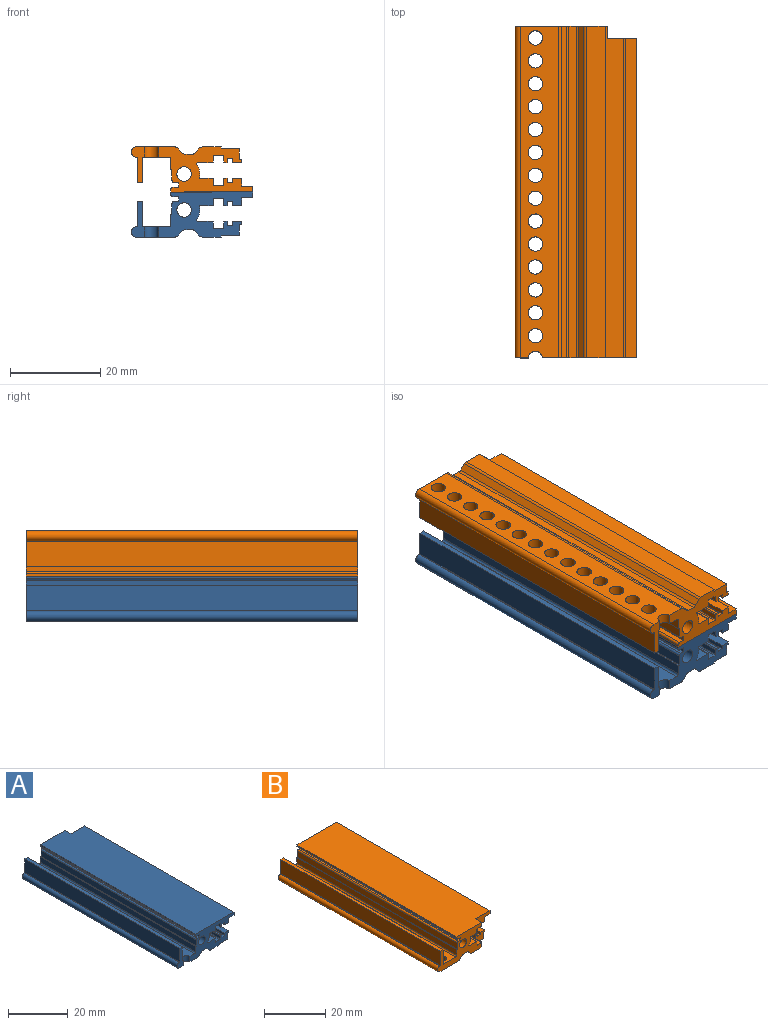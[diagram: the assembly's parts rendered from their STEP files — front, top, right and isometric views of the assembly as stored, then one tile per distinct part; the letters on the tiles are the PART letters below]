
ASSEMBLY  parts=2 mates=1
PART A: 86 faces, bbox 27x73.6x10 mm
  f0: plane 73.6x18.25mm, normal (0,0,1), area 1325mm2, adj f36,f57,f58,f59,f60,f62
  f1: cylinder r=1.6mm len=73.6mm, axis (0,1,0), area 739.9mm2, adj f36,f58
  f2: plane 73.6x1.13mm, normal (0.71,0,-0.71), area 117.8mm2, adj f3,f35,f36,f58
  f3: cylinder r=0.8mm len=73.6mm, axis (0,-1,0), area 46.2mm2, adj f2,f4,f36,f58
  f4: plane 73.6x1.64mm, normal (0,0,-1), area 120.5mm2, adj f3,f5,f36,f58
  f5: cylinder r=0.8mm len=73.6mm, axis (0,-1,0), area 46.2mm2, adj f4,f6,f36,f58
  f6: plane 73.6x1.13mm, normal (-0.71,0,-0.71), area 117.8mm2, adj f5,f36,f37,f58
  f7: cylinder r=1.6mm len=3.18mm, axis (0,0,-1), area 10.6mm2, adj f9,f38,f58,f85
  f8: plane 73.6x0.23mm, normal (0,0,1), area 16.6mm2, adj f10,f36,f55,f85
  f9: plane 73.6x5.7mm, normal (0,0,1), area 303.4mm2, adj f7,f11,f12,f36,f40,f41,f42,f43
  f10: plane 73.6x5.65mm, normal (-1,0,0), area 415.8mm2, adj f8,f36,f54,f85
  f11: plane 73.6x5.65mm, normal (1,0,0), area 415.8mm2, adj f9,f36,f54,f85
  f12: cylinder r=0.5mm len=73.6mm, axis (0,-1,0), area 57.8mm2, adj f9,f13,f36,f58
  f13: plane 73.6x2.25mm, normal (-1,0,0), area 165.6mm2, adj f12,f14,f36,f58
  f14: plane 73.6x0.3mm, normal (0,0,1), area 22.1mm2, adj f13,f15,f36,f58
  f15: plane 73.6x2.4mm, normal (-1,0,0), area 176.6mm2, adj f14,f16,f36,f58
  f16: cylinder r=0.5mm len=73.6mm, axis (0,-1,0), area 57.8mm2, adj f15,f17,f36,f58
  f17: plane 73.6x1mm, normal (0,0,1), area 73.6mm2, adj f16,f18,f36,f58
  f18: plane 73.6x1.1mm, normal (-1,0,0), area 81mm2, adj f17,f19,f36,f58
  f19: plane 73.6x1.3mm, normal (0,0,-1), area 95.7mm2, adj f18,f36,f56,f58
  f20: cylinder r=0.2mm len=73.6mm, axis (0,1,0), area 23.1mm2, adj f34,f36,f58,f62,f64
  f21: plane 73.6x4mm, normal (0,0,-1), area 284.6mm2, adj f22,f36,f58,f61,f63,f80
  f22: plane 73.6x0.4mm, normal (1,0,0), area 29.4mm2, adj f21,f36,f39,f58
  f23: cylinder r=0.2mm len=73.6mm, axis (0,1,0), area 23.1mm2, adj f24,f36,f58,f63,f82
  f24: plane 73.6x1.9mm, normal (0,0,1), area 139.8mm2, adj f23,f25,f36,f58
  f25: cylinder r=0.2mm len=73.6mm, axis (0,1,0), area 23.1mm2, adj f24,f26,f36,f58
  f26: plane 73.6x1.2mm, normal (1,0,0), area 88.3mm2, adj f25,f36,f58,f83
  f27: plane 73.6x3.31mm, normal (0,0,1), area 243.8mm2, adj f28,f36,f58,f83
  f28: cylinder r=0.2mm len=73.6mm, axis (0,1,0), area 32.7mm2, adj f27,f29,f36,f58
  f29: cylinder r=3.5mm len=73.6mm, axis (0,1,0), area 221mm2, adj f28,f30,f36,f58
  f30: cylinder r=0.2mm len=73.6mm, axis (0,1,0), area 26.1mm2, adj f29,f31,f36,f58
  f31: plane 73.6x2.63mm, normal (0,0,-1), area 193.3mm2, adj f30,f36,f58,f84
  f32: plane 73.6x1.2mm, normal (1,0,0), area 88.3mm2, adj f33,f36,f58,f84
  f33: cylinder r=0.2mm len=73.6mm, axis (0,1,0), area 23.1mm2, adj f32,f34,f36,f58
  f34: plane 73.6x1.9mm, normal (0,0,-1), area 139.8mm2, adj f20,f33,f36,f58
  f35: cylinder r=0.8mm len=73.6mm, axis (0,-1,0), area 46.2mm2, adj f2,f36,f38,f58
  f36: plane 20.5x10mm, normal (0,1,0), area 100.1mm2, adj f0,f1,f2,f3,f4,f5,f6,f8
  f37: cylinder r=0.8mm len=73.6mm, axis (0,1,0), area 46.2mm2, adj f6,f36,f39,f58
  f38: plane 73.6x8.54mm, normal (0,0,-1), area 512.7mm2, adj f7,f35,f36,f40,f41,f42,f43,f44
  f39: plane 73.6x4.17mm, normal (0,0,-1), area 306.8mm2, adj f22,f36,f37,f58
  f40: cylinder r=1.6mm len=3.2mm, axis (0,0,-1), area 22.6mm2, adj f9,f38
  f41: cylinder r=1.6mm len=3.2mm, axis (0,0,-1), area 22.6mm2, adj f9,f38
  f42: cylinder r=1.6mm len=3.2mm, axis (0,0,-1), area 22.6mm2, adj f9,f38
  f43: cylinder r=1.6mm len=3.2mm, axis (0,0,-1), area 22.6mm2, adj f9,f38
  f44: cylinder r=1.6mm len=3.2mm, axis (0,0,-1), area 22.6mm2, adj f9,f38
  f45: cylinder r=1.6mm len=3.2mm, axis (0,0,-1), area 22.6mm2, adj f9,f38
  f46: cylinder r=1.6mm len=3.2mm, axis (0,0,-1), area 22.6mm2, adj f9,f38
  f47: cylinder r=1.6mm len=3.2mm, axis (0,0,-1), area 22.6mm2, adj f9,f38
  f48: cylinder r=1.6mm len=3.2mm, axis (0,0,-1), area 22.6mm2, adj f9,f38
  f49: cylinder r=1.6mm len=3.2mm, axis (0,0,-1), area 22.6mm2, adj f9,f38
  f50: cylinder r=1.6mm len=3.2mm, axis (0,0,-1), area 22.6mm2, adj f9,f38
  f51: cylinder r=1.6mm len=3.2mm, axis (0,0,-1), area 22.6mm2, adj f9,f38
  f52: cylinder r=1.6mm len=3.2mm, axis (0,0,-1), area 22.6mm2, adj f9,f38
  f53: cylinder r=1.6mm len=3.2mm, axis (0,0,-1), area 22.6mm2, adj f9,f38
  f54: plane 73.6x1.2mm, normal (0,0,1), area 88.3mm2, adj f10,f11,f36,f85
  f55: cylinder r=1.12mm len=73.6mm, axis (0,-1,0), area 260.1mm2, adj f8,f36,f38,f85
  f56: cylinder r=0.5mm len=73.6mm, axis (0,1,0), area 57.8mm2, adj f19,f36,f57,f58
  f57: plane 73.6x0.5mm, normal (-1,0,0), area 36.8mm2, adj f0,f36,f56,f58
  f58: plane 20.91x10mm, normal (0,-1,0), area 104.8mm2, adj f0,f1,f2,f3,f4,f5,f6,f7
  f59: plane 70.8x1.3mm, normal (1,0,0), area 92mm2, adj f0,f58,f60,f78
  f60: plane 6.5x3.05mm, normal (0,1,0), area 14.4mm2, adj f0,f59,f62,f64,f65,f66,f67,f69
  f61: plane 4x3.15mm, normal (0,1,0), area 10.3mm2, adj f21,f63,f68,f70,f71,f73,f75,f77
  f62: plane 2.8x1.65mm, normal (1,0,0), area 4.6mm2, adj f0,f20,f36,f60
  f63: plane 2.8x1.75mm, normal (1,0,0), area 4.9mm2, adj f21,f23,f36,f61
  f64: plane 70.8x1.2mm, normal (-1,0,0), area 85mm2, adj f20,f58,f60,f65
  f65: cylinder r=0.2mm len=70.8mm, axis (0,1,0), area 22.2mm2, adj f58,f60,f64,f66
  f66: plane 70.8x0.6mm, normal (0,0,-1), area 42.5mm2, adj f58,f60,f65,f69
  f67: plane 70.8x2mm, normal (0,0,-1), area 141.6mm2, adj f58,f60,f72,f76
  f68: plane 70.8x0.9mm, normal (1,0,0), area 63.7mm2, adj f58,f61,f71,f75
  f69: plane 70.8x0.9mm, normal (1,0,0), area 63.7mm2, adj f58,f60,f66,f74
  f70: plane 70.8x2mm, normal (0,0,1), area 141.6mm2, adj f58,f61,f73,f77
  f71: plane 70.8x0.6mm, normal (0,0,1), area 42.5mm2, adj f58,f61,f68,f81
  f72: plane 70.8x0.9mm, normal (-1,0,0), area 63.7mm2, adj f58,f60,f67,f74
  f73: plane 70.8x0.9mm, normal (-1,0,0), area 63.7mm2, adj f58,f61,f70,f75
  f74: plane 70.8x1.2mm, normal (0,0,-1), area 85mm2, adj f58,f60,f69,f72
  f75: plane 70.8x1.2mm, normal (0,0,1), area 85mm2, adj f58,f61,f68,f73
  f76: plane 70.8x1.75mm, normal (1,0,0), area 123.9mm2, adj f58,f60,f67,f78
  f77: plane 70.8x0.75mm, normal (1,0,0), area 53.1mm2, adj f58,f61,f70,f79
  f78: plane 70.8x2.5mm, normal (0,0,-1), area 177mm2, adj f58,f59,f60,f76
  f79: plane 70.8x0.5mm, normal (0,0,-1), area 35.4mm2, adj f58,f61,f77,f80
  f80: plane 70.8x2.4mm, normal (1,0,0), area 169.9mm2, adj f21,f58,f61,f79
  f81: cylinder r=0.2mm len=70.8mm, axis (0,1,0), area 22.2mm2, adj f58,f61,f71,f82
  f82: plane 70.8x1.2mm, normal (-1,0,0), area 85mm2, adj f23,f58,f61,f81
  f83: cylinder r=0.2mm len=73.6mm, axis (0,1,0), area 23.1mm2, adj f26,f27,f36,f58
  f84: cylinder r=0.2mm len=73.6mm, axis (0,1,0), area 23.1mm2, adj f31,f32,f36,f58
  f85: plane 7.9x2.91mm, normal (0,-1,0), area 12.8mm2, adj f7,f8,f9,f10,f11,f38,f54,f55
PART B: 86 faces, bbox 27x73.6x10 mm
  f0: cylinder r=1.12mm len=73.6mm, axis (0,-1,0), area 260.1mm2, adj f3,f11,f14,f85
  f1: cylinder r=0.5mm len=73.6mm, axis (0,-1,0), area 57.8mm2, adj f3,f36,f37,f48
  f2: cylinder r=0.8mm len=73.6mm, axis (0,-1,0), area 46.2mm2, adj f3,f5,f11,f48
  f3: plane 20.5x10mm, normal (0,-1,0), area 100.1mm2, adj f0,f1,f2,f4,f5,f6,f7,f8
  f4: cylinder r=1.6mm len=73.6mm, axis (0,1,0), area 739.9mm2, adj f3,f48
  f5: plane 73.6x1.13mm, normal (0.71,0,-0.71), area 117.8mm2, adj f2,f3,f6,f48
  f6: cylinder r=0.8mm len=73.6mm, axis (0,-1,0), area 46.2mm2, adj f3,f5,f7,f48
  f7: plane 73.6x1.64mm, normal (0,0,-1), area 120.5mm2, adj f3,f6,f8,f48
  f8: cylinder r=0.8mm len=73.6mm, axis (0,-1,0), area 46.2mm2, adj f3,f7,f9,f48
  f9: plane 73.6x1.13mm, normal (-0.71,0,-0.71), area 117.8mm2, adj f3,f8,f10,f48
  f10: cylinder r=0.8mm len=73.6mm, axis (0,1,0), area 46.2mm2, adj f3,f9,f12,f48
  f11: plane 73.6x8.54mm, normal (0,0,-1), area 512.7mm2, adj f0,f2,f3,f13,f16,f17,f18,f19
  f12: plane 73.6x4.17mm, normal (0,0,-1), area 306.8mm2, adj f3,f10,f48,f68
  f13: cylinder r=1.6mm len=3.2mm, axis (0,0,-1), area 22.6mm2, adj f11,f15
  f14: plane 73.6x0.23mm, normal (0,0,1), area 16.6mm2, adj f0,f3,f30,f85
  f15: plane 73.6x5.7mm, normal (0,0,1), area 303.4mm2, adj f3,f13,f16,f17,f18,f19,f20,f21
  f16: cylinder r=1.6mm len=3.18mm, axis (0,0,-1), area 10.6mm2, adj f11,f15,f48,f85
  f17: cylinder r=1.6mm len=3.2mm, axis (0,0,-1), area 22.6mm2, adj f11,f15
  f18: cylinder r=1.6mm len=3.2mm, axis (0,0,-1), area 22.6mm2, adj f11,f15
  f19: cylinder r=1.6mm len=3.2mm, axis (0,0,-1), area 22.6mm2, adj f11,f15
  f20: cylinder r=1.6mm len=3.2mm, axis (0,0,-1), area 22.6mm2, adj f11,f15
  f21: cylinder r=1.6mm len=3.2mm, axis (0,0,-1), area 22.6mm2, adj f11,f15
  f22: cylinder r=1.6mm len=3.2mm, axis (0,0,-1), area 22.6mm2, adj f11,f15
  f23: cylinder r=1.6mm len=3.2mm, axis (0,0,-1), area 22.6mm2, adj f11,f15
  f24: cylinder r=1.6mm len=3.2mm, axis (0,0,-1), area 22.6mm2, adj f11,f15
  f25: cylinder r=1.6mm len=3.2mm, axis (0,0,-1), area 22.6mm2, adj f11,f15
  f26: cylinder r=1.6mm len=3.2mm, axis (0,0,-1), area 22.6mm2, adj f11,f15
  f27: cylinder r=1.6mm len=3.2mm, axis (0,0,-1), area 22.6mm2, adj f11,f15
  f28: cylinder r=1.6mm len=3.2mm, axis (0,0,-1), area 22.6mm2, adj f11,f15
  f29: cylinder r=1.6mm len=3.2mm, axis (0,0,-1), area 22.6mm2, adj f11,f15
  f30: plane 73.6x5.65mm, normal (-1,0,0), area 415.8mm2, adj f3,f14,f31,f85
  f31: plane 73.6x1.2mm, normal (0,0,1), area 88.3mm2, adj f3,f30,f32,f85
  f32: plane 73.6x5.65mm, normal (1,0,0), area 415.8mm2, adj f3,f15,f31,f85
  f33: cylinder r=0.5mm len=73.6mm, axis (0,-1,0), area 57.8mm2, adj f3,f15,f34,f48
  f34: plane 73.6x2.25mm, normal (-1,0,0), area 165.6mm2, adj f3,f33,f35,f48
  f35: plane 73.6x0.3mm, normal (0,0,1), area 22.1mm2, adj f3,f34,f36,f48
  f36: plane 73.6x2.4mm, normal (-1,0,0), area 176.6mm2, adj f1,f3,f35,f48
  f37: plane 73.6x1mm, normal (0,0,1), area 73.6mm2, adj f1,f3,f38,f48
  f38: plane 73.6x1.1mm, normal (-1,0,0), area 81mm2, adj f3,f37,f39,f48
  f39: plane 73.6x1.3mm, normal (0,0,-1), area 95.7mm2, adj f3,f38,f40,f48
  f40: cylinder r=0.5mm len=73.6mm, axis (0,1,0), area 57.8mm2, adj f3,f39,f41,f48
  f41: plane 73.6x0.5mm, normal (-1,0,0), area 36.8mm2, adj f3,f40,f42,f48
  f42: plane 73.6x18.25mm, normal (0,0,1), area 1325mm2, adj f3,f41,f43,f45,f47,f48
  f43: plane 2.8x1.65mm, normal (1,0,0), area 4.6mm2, adj f3,f42,f45,f49
  f44: plane 2.8x1.75mm, normal (1,0,0), area 4.9mm2, adj f3,f46,f67,f71
  f45: plane 6.5x3.05mm, normal (0,-1,0), area 14.4mm2, adj f42,f43,f47,f50,f51,f52,f53,f55
  f46: plane 4x3.15mm, normal (0,-1,0), area 10.3mm2, adj f44,f54,f56,f57,f59,f61,f63,f65
  f47: plane 70.8x1.3mm, normal (1,0,0), area 92mm2, adj f42,f45,f48,f64
  f48: plane 20.91x10mm, normal (0,1,0), area 104.8mm2, adj f1,f2,f4,f5,f6,f7,f8,f9
  f49: cylinder r=0.2mm len=73.6mm, axis (0,1,0), area 23.1mm2, adj f3,f43,f48,f50,f84
  f50: plane 70.8x1.2mm, normal (-1,0,0), area 85mm2, adj f45,f48,f49,f51
  f51: cylinder r=0.2mm len=70.8mm, axis (0,1,0), area 22.2mm2, adj f45,f48,f50,f52
  f52: plane 70.8x0.6mm, normal (0,0,-1), area 42.5mm2, adj f45,f48,f51,f55
  f53: plane 70.8x2mm, normal (0,0,-1), area 141.6mm2, adj f45,f48,f58,f62
  f54: plane 70.8x0.9mm, normal (1,0,0), area 63.7mm2, adj f46,f48,f57,f61
  f55: plane 70.8x0.9mm, normal (1,0,0), area 63.7mm2, adj f45,f48,f52,f60
  f56: plane 70.8x2mm, normal (0,0,1), area 141.6mm2, adj f46,f48,f59,f63
  f57: plane 70.8x0.6mm, normal (0,0,1), area 42.5mm2, adj f46,f48,f54,f69
  f58: plane 70.8x0.9mm, normal (-1,0,0), area 63.7mm2, adj f45,f48,f53,f60
  f59: plane 70.8x0.9mm, normal (-1,0,0), area 63.7mm2, adj f46,f48,f56,f61
  f60: plane 70.8x1.2mm, normal (0,0,-1), area 85mm2, adj f45,f48,f55,f58
  f61: plane 70.8x1.2mm, normal (0,0,1), area 85mm2, adj f46,f48,f54,f59
  f62: plane 70.8x1.75mm, normal (1,0,0), area 123.9mm2, adj f45,f48,f53,f64
  f63: plane 70.8x0.75mm, normal (1,0,0), area 53.1mm2, adj f46,f48,f56,f65
  f64: plane 70.8x2.5mm, normal (0,0,-1), area 177mm2, adj f45,f47,f48,f62
  f65: plane 70.8x0.5mm, normal (0,0,-1), area 35.4mm2, adj f46,f48,f63,f66
  f66: plane 70.8x2.4mm, normal (1,0,0), area 169.9mm2, adj f46,f48,f65,f67
  f67: plane 73.6x4mm, normal (0,0,-1), area 284.6mm2, adj f3,f44,f46,f48,f66,f68
  f68: plane 73.6x0.4mm, normal (1,0,0), area 29.4mm2, adj f3,f12,f48,f67
  f69: cylinder r=0.2mm len=70.8mm, axis (0,1,0), area 22.2mm2, adj f46,f48,f57,f70
  f70: plane 70.8x1.2mm, normal (-1,0,0), area 85mm2, adj f46,f48,f69,f71
  f71: cylinder r=0.2mm len=73.6mm, axis (0,1,0), area 23.1mm2, adj f3,f44,f48,f70,f72
  f72: plane 73.6x1.9mm, normal (0,0,1), area 139.8mm2, adj f3,f48,f71,f73
  f73: cylinder r=0.2mm len=73.6mm, axis (0,1,0), area 23.1mm2, adj f3,f48,f72,f74
  f74: plane 73.6x1.2mm, normal (1,0,0), area 88.3mm2, adj f3,f48,f73,f75
  f75: cylinder r=0.2mm len=73.6mm, axis (0,1,0), area 23.1mm2, adj f3,f48,f74,f76
  f76: plane 73.6x3.31mm, normal (0,0,1), area 243.8mm2, adj f3,f48,f75,f77
  f77: cylinder r=0.2mm len=73.6mm, axis (0,1,0), area 32.7mm2, adj f3,f48,f76,f78
  f78: cylinder r=3.5mm len=73.6mm, axis (0,1,0), area 221mm2, adj f3,f48,f77,f79
  f79: cylinder r=0.2mm len=73.6mm, axis (0,1,0), area 26.1mm2, adj f3,f48,f78,f80
  f80: plane 73.6x2.63mm, normal (0,0,-1), area 193.3mm2, adj f3,f48,f79,f81
  f81: cylinder r=0.2mm len=73.6mm, axis (0,1,0), area 23.1mm2, adj f3,f48,f80,f82
  f82: plane 73.6x1.2mm, normal (1,0,0), area 88.3mm2, adj f3,f48,f81,f83
  f83: cylinder r=0.2mm len=73.6mm, axis (0,1,0), area 23.1mm2, adj f3,f48,f82,f84
  f84: plane 73.6x1.9mm, normal (0,0,-1), area 139.8mm2, adj f3,f48,f49,f83
  f85: plane 7.9x2.91mm, normal (0,1,0), area 12.8mm2, adj f0,f11,f14,f15,f16,f30,f31,f32
PLACE A t=(8.38,-0.03,26.3)mm
PLACE B rot(axis=(1,0,0),180deg) t=(8.38,-0.03,34.3)mm
MATE fastened A.f0 <-> B.f42  axis (0,0,1) through (14.43,0.88,30.3)mm
